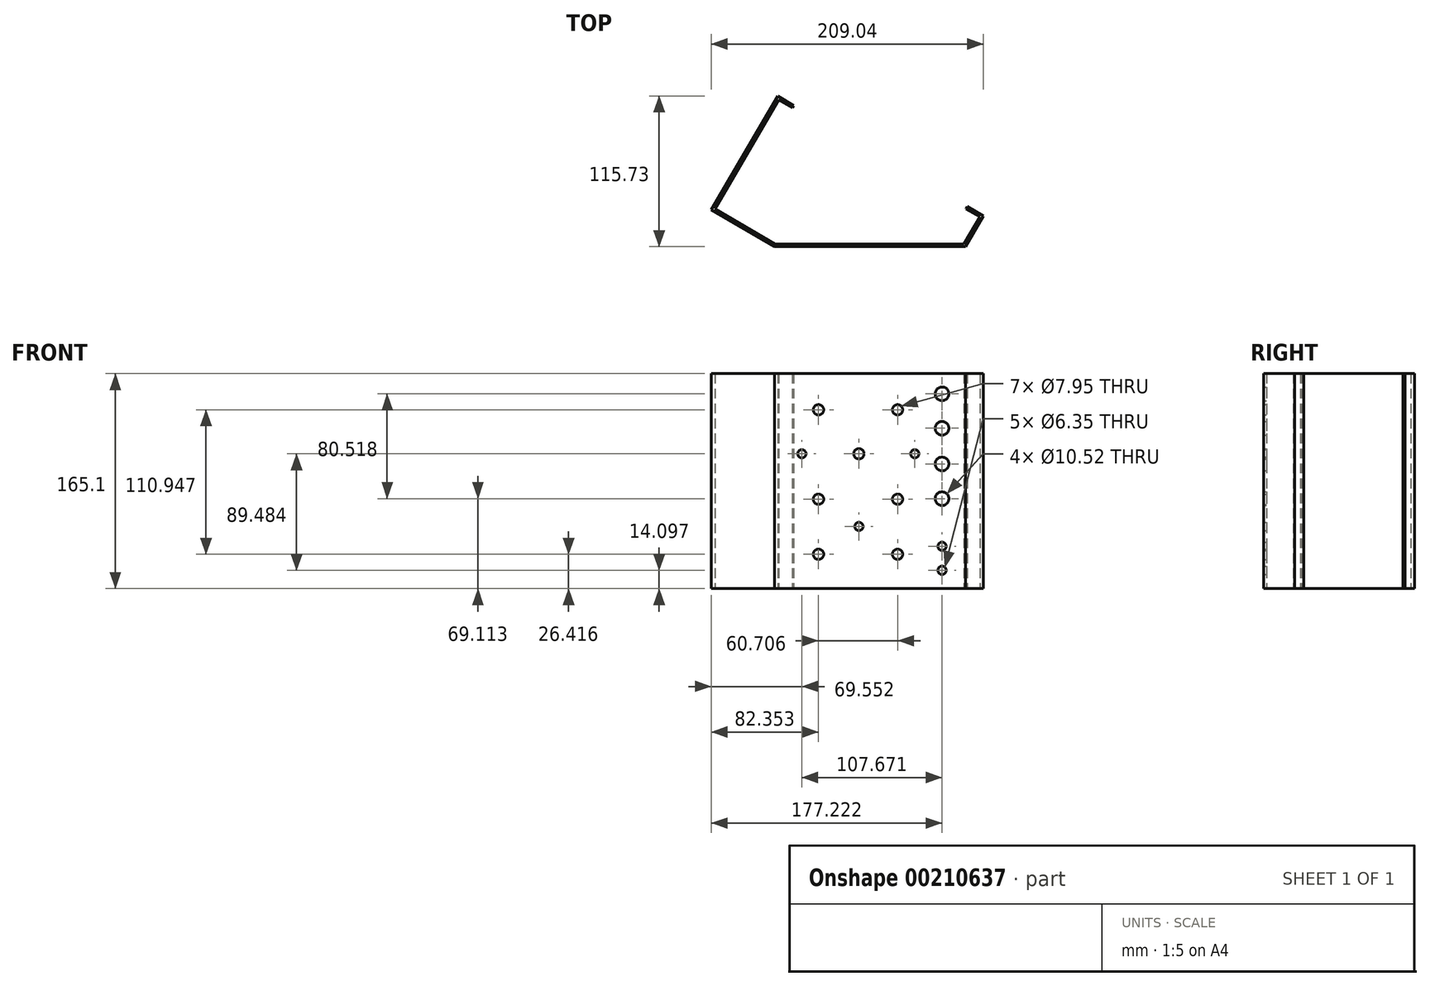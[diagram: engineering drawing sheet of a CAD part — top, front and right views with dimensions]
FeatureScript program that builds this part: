
annotation { "Feature Type Name" : "Feature", "Feature Type Description" : "" }
export const myFeature = defineFeature(function(context is Context, id is Id, definition is map)
    precondition{}
    {
        {
            var Q0;
            Q0=qCreatedBy(makeId("Top.planeOp"),FACE);
            var sketch = newSketch(context, id + "F0", { "sketchPlane" : qUnion([Q0])});
            skLineSegment(sketch, "E0", {"start": v(0, 0) * mm, "end": v(146.79, 0) * mm});
            skLineSegment(sketch, "E1", {"start": v(146.79, 0) * mm, "end": v(160.56, 23.64) * mm});
            skLineSegment(sketch, "E2", {"start": v(160.56, 23.64) * mm, "end": v(148.18, 30.85) * mm});
            skLineSegment(sketch, "E3", {"start": v(0, 0) * mm, "end": v(-48.48, 28.24) * mm});
            skLineSegment(sketch, "E4", {"start": v(-48.48, 28.24) * mm, "end": v(2.48, 115.73) * mm});
            skLineSegment(sketch, "E5", {"start": v(2.48, 115.73) * mm, "end": v(14.86, 108.51) * mm});
            skLineSegment(sketch, "E6", {"start": v(14.86, 108.51) * mm, "end": v(148.18, 30.85) * mm, "construction": true});
            skLineSegment(sketch, "E7.0", {"start": v(3.2, 112.98) * mm, "end": v(13.84, 106.79) * mm});
            skLineSegment(sketch, "E7.1", {"start": v(-45.74, 28.97) * mm, "end": v(3.2, 112.98) * mm});
            skLineSegment(sketch, "E7.2", {"start": v(157.81, 22.91) * mm, "end": v(147.16, 29.12) * mm});
            skLineSegment(sketch, "E7.3", {"start": v(145.63, 2) * mm, "end": v(157.81, 22.91) * mm});
            skLineSegment(sketch, "E7.4", {"start": v(0.54, 2) * mm, "end": v(145.63, 2) * mm});
            skLineSegment(sketch, "E7.5", {"start": v(0.54, 2) * mm, "end": v(-45.74, 28.97) * mm});
            skLineSegment(sketch, "E8", {"start": v(14.86, 108.51) * mm, "end": v(13.84, 106.79) * mm});
            skLineSegment(sketch, "E9", {"start": v(148.18, 30.85) * mm, "end": v(147.16, 29.12) * mm});
            skSolve(sketch);
        }
        {
            var Q0;
            Q0 = qSketchRegion(id + "F0", true);
            extrude(context, id + "F1", {"entities" : qUnion([Q0]), "depth" : 165.1 * mm});
        }
        {
            var Q0;
            Q0=makeQuery(id+"F1.opExtrude","SWEPT_FACE",FACE,{"disambiguationData":[OSD([sQuery(id+"F0.wireOp",EDGE,"E7.4")])]});
            var sketch = newSketch(context, id + "F2", { "sketchPlane" : qUnion([Q0])});
            skLineSegment(sketch, "E10.0", {"start": v(-0.54, 0) * mm, "end": v(-145.63, 0) * mm, "construction": true});
            skLineSegment(sketch, "E11.0", {"start": v(-0.54, 165.1) * mm, "end": v(-0.54, 0) * mm, "construction": true});
            skLineSegment(sketch, "E12.0", {"start": v(-0.54, 165.1) * mm, "end": v(-145.63, 165.1) * mm, "construction": true});
            skLineSegment(sketch, "E13.0", {"start": v(-145.63, 165.1) * mm, "end": v(-145.63, 0) * mm, "construction": true});
            skCircle(sketch, "E14", {"center": v(-128.74, 14.1) * mm, "radius": 3.18 * mm});
            skCircle(sketch, "E15", {"center": v(-128.74, 32.54) * mm, "radius": 3.18 * mm});
            skCircle(sketch, "E16", {"center": v(-128.74, 69.11) * mm, "radius": 5.26 * mm});
            skCircle(sketch, "E17", {"center": v(-128.74, 95.78) * mm, "radius": 5.26 * mm});
            skCircle(sketch, "E18", {"center": v(-128.74, 123.22) * mm, "radius": 5.26 * mm});
            skCircle(sketch, "E19", {"center": v(-128.74, 149.63) * mm, "radius": 5.26 * mm});
            skLineSegment(sketch, "E20", {"start": v(-128.74, 95.78) * mm, "end": v(-145.63, 95.78) * mm, "construction": true});
            skLineSegment(sketch, "E21", {"start": v(-128.74, 123.22) * mm, "end": v(-145.63, 123.22) * mm, "construction": true});
            skLineSegment(sketch, "E22", {"start": v(-128.74, 149.63) * mm, "end": v(-145.63, 149.63) * mm, "construction": true});
            skLineSegment(sketch, "E23", {"start": v(-128.74, 69.11) * mm, "end": v(-145.63, 69.11) * mm, "construction": true});
            skCircle(sketch, "E24", {"center": v(-107.81, 103.58) * mm, "radius": 3.18 * mm});
            skCircle(sketch, "E25", {"center": v(-94.58, 26.42) * mm, "radius": 3.98 * mm});
            skLineSegment(sketch, "E26", {"start": v(-94.58, 26.42) * mm, "end": v(-145.63, 26.42) * mm, "construction": true});
            skCircle(sketch, "E27", {"center": v(-94.58, 68.7) * mm, "radius": 3.98 * mm});
            skLineSegment(sketch, "E28", {"start": v(-94.58, 68.7) * mm, "end": v(-145.63, 68.7) * mm, "construction": true});
            skCircle(sketch, "E29", {"center": v(-94.58, 137.36) * mm, "radius": 3.98 * mm});
            skLineSegment(sketch, "E30", {"start": v(-94.58, 137.36) * mm, "end": v(-145.63, 137.36) * mm, "construction": true});
            skCircle(sketch, "E31", {"center": v(-64.89, 47.78) * mm, "radius": 3.18 * mm});
            skLineSegment(sketch, "E32", {"start": v(-64.89, 47.78) * mm, "end": v(-145.63, 47.78) * mm, "construction": true});
            skCircle(sketch, "E33", {"center": v(-64.89, 103.58) * mm, "radius": 3.98 * mm});
            skLineSegment(sketch, "E34", {"start": v(-64.89, 103.58) * mm, "end": v(-145.63, 103.58) * mm, "construction": true});
            skCircle(sketch, "E35", {"center": v(-33.87, 26.42) * mm, "radius": 3.98 * mm});
            skCircle(sketch, "E36", {"center": v(-33.87, 68.7) * mm, "radius": 3.98 * mm});
            skCircle(sketch, "E37", {"center": v(-33.87, 137.36) * mm, "radius": 3.98 * mm});
            skLineSegment(sketch, "E38", {"start": v(-33.87, 26.42) * mm, "end": v(-145.63, 26.42) * mm, "construction": true});
            skLineSegment(sketch, "E39", {"start": v(-33.87, 68.7) * mm, "end": v(-145.63, 68.7) * mm, "construction": true});
            skLineSegment(sketch, "E40", {"start": v(-33.87, 137.36) * mm, "end": v(-145.63, 137.36) * mm, "construction": true});
            skCircle(sketch, "E41", {"center": v(-21.07, 103.58) * mm, "radius": 3.18 * mm});
            skSolve(sketch);
        }
        {
            var Q0;
            Q0 = qSketchRegion(id + "F2", true);
            extrude(context, id + "F3", {"entities" : qUnion([Q0]), "operationType" : NewBodyOperationType.REMOVE, "endBound" : BoundingType.UP_TO_NEXT, "oppositeDirection" : true, "depth" : 25.4 * mm});
        }
    });
